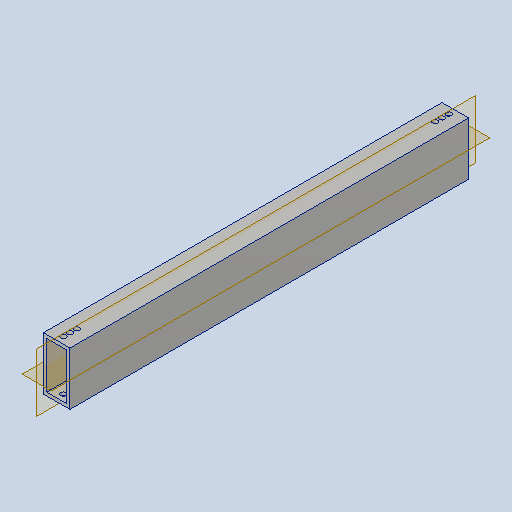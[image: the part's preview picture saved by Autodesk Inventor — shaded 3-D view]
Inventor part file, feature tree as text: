
AUTODESK INVENTOR PART (.ipt)
format: ipt  version: 2023.4 (Build 274418000, 418)  size: 266,240 bytes
history: native  units: in
note: dims shown in document units (in); Inventor stores cm internally (conversion verified against a paired STEP export)
features: extrude x1, hole x1, sketch x1
ambient origin geometry x8: Origin, YZ Plane, XZ Plane, XY Plane, X Axis, Y Axis, Z Axis, Center Point
bodies: Solid1 (feature_tree)
feature tree (3):
  extrude  "Extrusion1"  Depth=1.0in
  hole  "Hole1"  [1 undecoded]
  sketch  "Sketch2"  dims[d4=0.0in d5=0.25in d6=0.25in d7=0.25in d8=0.5in d9=0.201in d10=0.75in d11=0.385in d12=0.25in d13=0.5635in d14=1.0in d15=0.8108in d16=0.5in d17=0.25in d18=0.25in d19=0.25in]
note: 1 required parameter value undecoded (feature->parameter linkage not recoverable at this tier; creation-order binding heuristic only, values carry confidence <= 0.55)
